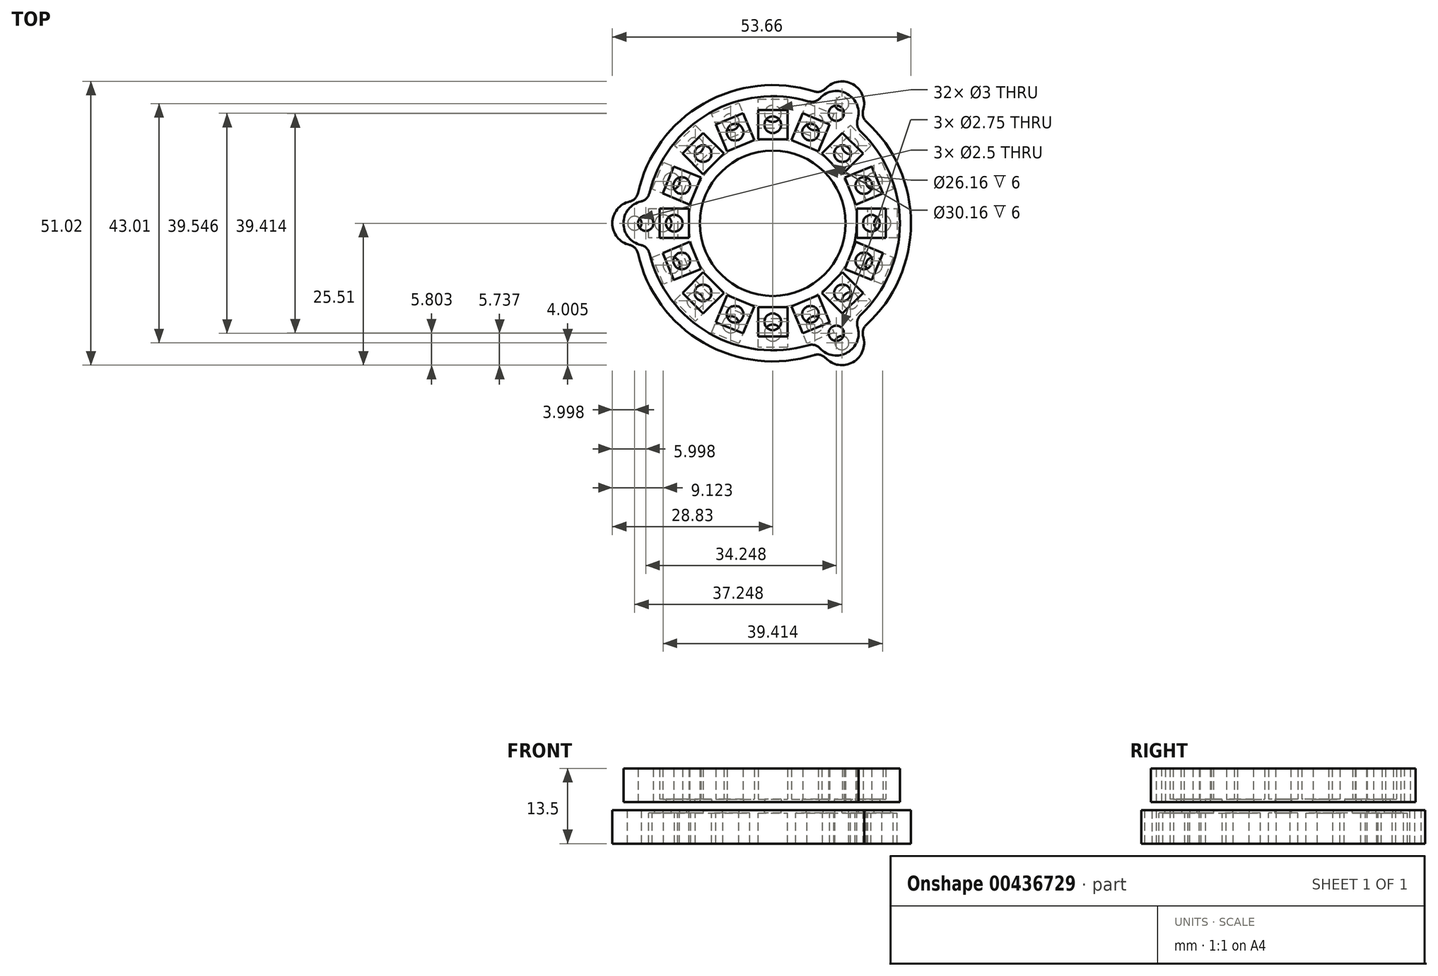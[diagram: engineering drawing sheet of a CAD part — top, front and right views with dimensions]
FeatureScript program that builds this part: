
annotation { "Feature Type Name" : "Feature", "Feature Type Description" : "" }
export const myFeature = defineFeature(function(context is Context, id is Id, definition is map)
    precondition{}
    {
        {
            var Q0;
            Q0=qCreatedBy(makeId("Top.planeOp"),FACE);
            var sketch = newSketch(context, id + "F0", { "sketchPlane" : qUnion([Q0])});
            skCircle(sketch, "E0.cCircle", {"center": v(0, 0) * mm, "radius": 15.08 * mm, "construction": true});
            skLineSegment(sketch, "E0.0", {"start": v(15.08, 3) * mm, "end": v(15.08, -3) * mm, "construction": true});
            skLineSegment(sketch, "E0.1", {"start": v(15.08, -3) * mm, "end": v(12.79, -8.54) * mm, "construction": true});
            skLineSegment(sketch, "E0.2", {"start": v(12.79, -8.54) * mm, "end": v(8.54, -12.79) * mm, "construction": true});
            skLineSegment(sketch, "E0.3", {"start": v(8.54, -12.79) * mm, "end": v(3, -15.08) * mm, "construction": true});
            skLineSegment(sketch, "E0.4", {"start": v(3, -15.08) * mm, "end": v(-3, -15.08) * mm, "construction": true});
            skLineSegment(sketch, "E0.5", {"start": v(-3, -15.08) * mm, "end": v(-8.54, -12.79) * mm, "construction": true});
            skLineSegment(sketch, "E0.6", {"start": v(-8.54, -12.79) * mm, "end": v(-12.79, -8.54) * mm, "construction": true});
            skLineSegment(sketch, "E0.7", {"start": v(-12.79, -8.54) * mm, "end": v(-15.08, -3) * mm, "construction": true});
            skLineSegment(sketch, "E0.8", {"start": v(-15.08, -3) * mm, "end": v(-15.08, 3) * mm, "construction": true});
            skLineSegment(sketch, "E0.9", {"start": v(-15.08, 3) * mm, "end": v(-12.79, 8.54) * mm, "construction": true});
            skLineSegment(sketch, "E0.10", {"start": v(-12.79, 8.54) * mm, "end": v(-8.54, 12.79) * mm, "construction": true});
            skLineSegment(sketch, "E0.11", {"start": v(-8.54, 12.79) * mm, "end": v(-3, 15.08) * mm, "construction": true});
            skLineSegment(sketch, "E0.12", {"start": v(-3, 15.08) * mm, "end": v(3, 15.08) * mm, "construction": true});
            skLineSegment(sketch, "E0.13", {"start": v(3, 15.08) * mm, "end": v(8.54, 12.79) * mm, "construction": true});
            skLineSegment(sketch, "E0.14", {"start": v(8.54, 12.79) * mm, "end": v(12.79, 8.54) * mm, "construction": true});
            skLineSegment(sketch, "E0.15", {"start": v(12.79, 8.54) * mm, "end": v(15.08, 3) * mm, "construction": true});
            skPoint(sketch, "E0.0.midPoint", {"position": v(15.08, 0) * mm});
            skLineSegment(sketch, "E1", {"start": v(13.6, 0) * mm, "end": v(23.93, 0) * mm, "construction": true});
            skLineSegment(sketch, "E2", {"start": v(15.08, 2.62) * mm, "end": v(20.33, 2.62) * mm, "construction": true});
            skLineSegment(sketch, "E3", {"start": v(20.33, 2.62) * mm, "end": v(20.33, -2.62) * mm, "construction": true});
            skLineSegment(sketch, "E4", {"start": v(20.33, -2.62) * mm, "end": v(15.08, -2.62) * mm, "construction": true});
            skLineSegment(sketch, "E5", {"start": v(17.08, 2.62) * mm, "end": v(22.33, 2.62) * mm, "construction": true});
            skLineSegment(sketch, "E6", {"start": v(22.33, 2.62) * mm, "end": v(22.33, -2.62) * mm, "construction": true});
            skLineSegment(sketch, "E7", {"start": v(22.33, -2.62) * mm, "end": v(17.08, -2.62) * mm, "construction": true});
            skLineSegment(sketch, "E8", {"start": v(17.08, -2.62) * mm, "end": v(17.08, 2.62) * mm, "construction": true});
            skSolve(sketch);
        }
        {
            var Q0;
            Q0=qCreatedBy(makeId("Top.planeOp"),FACE);
            cPlane(context, id + "F1", {"entities" : qUnion([Q0]), "cplaneType" : CPlaneType.OFFSET, "offset" : 0.5 * mm, "oppositeDirection" : true, "width" : 150 * mm, "height" : 150 * mm});
        }
        {
            var Q0;
            Q0=qCreatedBy(id+"F1.planeOp",FACE);
            var sketch = newSketch(context, id + "F2", { "sketchPlane" : qUnion([Q0])});
            skCircle(sketch, "E9", {"center": v(-22.83, 0) * mm, "radius": 1.38 * mm});
            skArc(sketch, "E10", {"start": v(-22.48, 3.98) * mm, "mid": v(-26.83, 0) * mm, "end": v(-22.48, -3.98) * mm});
            skCircle(sketch, "E11", {"center": v(17.7, 0) * mm, "radius": 1.5 * mm});
            skCircle(sketch, "E12.1.0", {"center": v(16.36, -6.78) * mm, "radius": 1.5 * mm});
            skCircle(sketch, "E12.2.0", {"center": v(12.52, -12.52) * mm, "radius": 1.5 * mm});
            skCircle(sketch, "E12.3.0", {"center": v(6.78, -16.36) * mm, "radius": 1.5 * mm});
            skCircle(sketch, "E12.4.0", {"center": v(0, -17.7) * mm, "radius": 1.5 * mm});
            skCircle(sketch, "E12.5.0", {"center": v(-6.78, -16.36) * mm, "radius": 1.5 * mm});
            skCircle(sketch, "E12.6.0", {"center": v(-12.52, -12.52) * mm, "radius": 1.5 * mm});
            skCircle(sketch, "E12.7.0", {"center": v(-16.36, -6.78) * mm, "radius": 1.5 * mm});
            skCircle(sketch, "E12.8.0", {"center": v(-17.7, 0) * mm, "radius": 1.5 * mm});
            skCircle(sketch, "E12.9.0", {"center": v(-16.36, 6.78) * mm, "radius": 1.5 * mm});
            skCircle(sketch, "E12.10.0", {"center": v(-12.52, 12.52) * mm, "radius": 1.5 * mm});
            skCircle(sketch, "E12.11.0", {"center": v(-6.78, 16.36) * mm, "radius": 1.5 * mm});
            skCircle(sketch, "E12.12.0", {"center": v(0, 17.7) * mm, "radius": 1.5 * mm});
            skCircle(sketch, "E12.13.0", {"center": v(6.78, 16.36) * mm, "radius": 1.5 * mm});
            skCircle(sketch, "E12.14.0", {"center": v(12.52, 12.52) * mm, "radius": 1.5 * mm});
            skCircle(sketch, "E12.15.0", {"center": v(16.36, 6.78) * mm, "radius": 1.5 * mm});
            skLineSegment(sketch, "E12.anchor1", {"start": v(0, 0) * mm, "end": v(17.7, 0) * mm, "construction": true});
            skLineSegment(sketch, "E12.anchor2", {"start": v(0, 0) * mm, "end": v(16.36, 6.78) * mm, "construction": true});
            skCircle(sketch, "E13.1.0", {"center": v(11.42, -19.77) * mm, "radius": 1.38 * mm});
            skArc(sketch, "E13.1.1", {"start": v(7.8, -21.46) * mm, "mid": v(13.42, -23.24) * mm, "end": v(14.7, -17.48) * mm});
            skCircle(sketch, "E13.2.0", {"center": v(11.42, 19.77) * mm, "radius": 1.38 * mm});
            skArc(sketch, "E13.2.1", {"start": v(14.7, 17.48) * mm, "mid": v(13.42, 23.24) * mm, "end": v(7.8, 21.46) * mm});
            skPoint(sketch, "E13.center", {"position": v(0, 0) * mm});
            skCircle(sketch, "E14", {"center": v(0, 0) * mm, "radius": 13.08 * mm});
            skArc(sketch, "E15.trimOffspring", {"start": v(-22.48, -3.98) * mm, "mid": v(-11.42, -19.77) * mm, "end": v(7.8, -21.46) * mm});
            skArc(sketch, "E16.trimOffspring", {"start": v(14.7, -17.48) * mm, "mid": v(22.83, 0) * mm, "end": v(14.7, 17.48) * mm});
            skArc(sketch, "E17.trimOffspring", {"start": v(7.8, 21.46) * mm, "mid": v(-11.42, 19.77) * mm, "end": v(-22.48, 3.98) * mm});
            skSolve(sketch);
        }
        {
            var Q0;
            Q0=qSketchRegion(id+"F2",true);
            extrude(context, id + "F3", {"entities" : qUnion([Q0]), "depth" : 6 * mm, "offsetDistance" : 25 * mm});
        }
        {
            var Q0;
            Q0=qCreatedBy(makeId("Top.planeOp"),FACE);
            var sketch = newSketch(context, id + "F4", { "sketchPlane" : qUnion([Q0])});
            skLineSegment(sketch, "E18.0", {"start": v(15.08, 2.62) * mm, "end": v(20.33, 2.62) * mm});
            skLineSegment(sketch, "E19.0", {"start": v(20.33, 2.62) * mm, "end": v(20.33, -2.62) * mm});
            skLineSegment(sketch, "E20.0", {"start": v(20.33, -2.62) * mm, "end": v(15.08, -2.62) * mm});
            skLineSegment(sketch, "E21", {"start": v(15.08, 2.62) * mm, "end": v(15.08, -2.62) * mm});
            skLineSegment(sketch, "E22.1.0", {"start": v(12.93, 8.2) * mm, "end": v(17.78, 10.2) * mm});
            skLineSegment(sketch, "E22.1.1", {"start": v(12.93, 8.2) * mm, "end": v(14.94, 3.35) * mm});
            skLineSegment(sketch, "E22.1.2", {"start": v(19.79, 5.36) * mm, "end": v(14.94, 3.35) * mm});
            skLineSegment(sketch, "E22.1.3", {"start": v(17.78, 10.2) * mm, "end": v(19.79, 5.36) * mm});
            skLineSegment(sketch, "E22.2.0", {"start": v(8.8, 12.52) * mm, "end": v(12.52, 16.23) * mm});
            skLineSegment(sketch, "E22.2.1", {"start": v(8.8, 12.52) * mm, "end": v(12.52, 8.8) * mm});
            skLineSegment(sketch, "E22.2.2", {"start": v(16.23, 12.52) * mm, "end": v(12.52, 8.8) * mm});
            skLineSegment(sketch, "E22.2.3", {"start": v(12.52, 16.23) * mm, "end": v(16.23, 12.52) * mm});
            skLineSegment(sketch, "E22.3.0", {"start": v(3.35, 14.94) * mm, "end": v(5.36, 19.79) * mm});
            skLineSegment(sketch, "E22.3.1", {"start": v(3.35, 14.94) * mm, "end": v(8.2, 12.93) * mm});
            skLineSegment(sketch, "E22.3.2", {"start": v(10.2, 17.78) * mm, "end": v(8.2, 12.93) * mm});
            skLineSegment(sketch, "E22.3.3", {"start": v(5.36, 19.79) * mm, "end": v(10.2, 17.78) * mm});
            skLineSegment(sketch, "E22.4.0", {"start": v(-2.62, 15.08) * mm, "end": v(-2.62, 20.33) * mm});
            skLineSegment(sketch, "E22.4.1", {"start": v(-2.62, 15.08) * mm, "end": v(2.63, 15.08) * mm});
            skLineSegment(sketch, "E22.4.2", {"start": v(2.62, 20.33) * mm, "end": v(2.63, 15.08) * mm});
            skLineSegment(sketch, "E22.4.3", {"start": v(-2.62, 20.33) * mm, "end": v(2.63, 20.33) * mm});
            skLineSegment(sketch, "E22.5.0", {"start": v(-8.2, 12.93) * mm, "end": v(-10.2, 17.78) * mm});
            skLineSegment(sketch, "E22.5.1", {"start": v(-8.2, 12.93) * mm, "end": v(-3.35, 14.94) * mm});
            skLineSegment(sketch, "E22.5.2", {"start": v(-5.36, 19.79) * mm, "end": v(-3.35, 14.94) * mm});
            skLineSegment(sketch, "E22.5.3", {"start": v(-10.2, 17.78) * mm, "end": v(-5.36, 19.79) * mm});
            skLineSegment(sketch, "E22.6.0", {"start": v(-12.52, 8.8) * mm, "end": v(-16.23, 12.52) * mm});
            skLineSegment(sketch, "E22.6.1", {"start": v(-12.52, 8.8) * mm, "end": v(-8.8, 12.52) * mm});
            skLineSegment(sketch, "E22.6.2", {"start": v(-12.52, 16.23) * mm, "end": v(-8.8, 12.52) * mm});
            skLineSegment(sketch, "E22.6.3", {"start": v(-16.23, 12.52) * mm, "end": v(-12.52, 16.23) * mm});
            skLineSegment(sketch, "E22.7.0", {"start": v(-14.94, 3.35) * mm, "end": v(-19.79, 5.36) * mm});
            skLineSegment(sketch, "E22.7.1", {"start": v(-14.94, 3.35) * mm, "end": v(-12.93, 8.2) * mm});
            skLineSegment(sketch, "E22.7.2", {"start": v(-17.78, 10.2) * mm, "end": v(-12.93, 8.2) * mm});
            skLineSegment(sketch, "E22.7.3", {"start": v(-19.79, 5.36) * mm, "end": v(-17.78, 10.2) * mm});
            skLineSegment(sketch, "E22.8.0", {"start": v(-15.08, -2.62) * mm, "end": v(-20.33, -2.62) * mm});
            skLineSegment(sketch, "E22.8.1", {"start": v(-15.08, -2.62) * mm, "end": v(-15.08, 2.63) * mm});
            skLineSegment(sketch, "E22.8.2", {"start": v(-20.33, 2.63) * mm, "end": v(-15.08, 2.63) * mm});
            skLineSegment(sketch, "E22.8.3", {"start": v(-20.33, -2.62) * mm, "end": v(-20.33, 2.63) * mm});
            skLineSegment(sketch, "E22.9.0", {"start": v(-12.93, -8.2) * mm, "end": v(-17.78, -10.2) * mm});
            skLineSegment(sketch, "E22.9.1", {"start": v(-12.93, -8.2) * mm, "end": v(-14.94, -3.35) * mm});
            skLineSegment(sketch, "E22.9.2", {"start": v(-19.79, -5.36) * mm, "end": v(-14.94, -3.35) * mm});
            skLineSegment(sketch, "E22.9.3", {"start": v(-17.78, -10.2) * mm, "end": v(-19.79, -5.36) * mm});
            skLineSegment(sketch, "E22.10.0", {"start": v(-8.8, -12.52) * mm, "end": v(-12.52, -16.23) * mm});
            skLineSegment(sketch, "E22.10.1", {"start": v(-8.8, -12.52) * mm, "end": v(-12.52, -8.8) * mm});
            skLineSegment(sketch, "E22.10.2", {"start": v(-16.23, -12.52) * mm, "end": v(-12.52, -8.8) * mm});
            skLineSegment(sketch, "E22.10.3", {"start": v(-12.52, -16.23) * mm, "end": v(-16.23, -12.52) * mm});
            skLineSegment(sketch, "E22.11.0", {"start": v(-3.35, -14.94) * mm, "end": v(-5.36, -19.79) * mm});
            skLineSegment(sketch, "E22.11.1", {"start": v(-3.35, -14.94) * mm, "end": v(-8.2, -12.93) * mm});
            skLineSegment(sketch, "E22.11.2", {"start": v(-10.2, -17.78) * mm, "end": v(-8.2, -12.93) * mm});
            skLineSegment(sketch, "E22.11.3", {"start": v(-5.36, -19.79) * mm, "end": v(-10.2, -17.78) * mm});
            skLineSegment(sketch, "E22.12.0", {"start": v(2.62, -15.08) * mm, "end": v(2.62, -20.33) * mm});
            skLineSegment(sketch, "E22.12.1", {"start": v(2.62, -15.08) * mm, "end": v(-2.63, -15.08) * mm});
            skLineSegment(sketch, "E22.12.2", {"start": v(-2.63, -20.33) * mm, "end": v(-2.63, -15.08) * mm});
            skLineSegment(sketch, "E22.12.3", {"start": v(2.62, -20.33) * mm, "end": v(-2.63, -20.33) * mm});
            skLineSegment(sketch, "E22.13.0", {"start": v(8.2, -12.93) * mm, "end": v(10.2, -17.78) * mm});
            skLineSegment(sketch, "E22.13.1", {"start": v(8.2, -12.93) * mm, "end": v(3.35, -14.94) * mm});
            skLineSegment(sketch, "E22.13.2", {"start": v(5.36, -19.79) * mm, "end": v(3.35, -14.94) * mm});
            skLineSegment(sketch, "E22.13.3", {"start": v(10.2, -17.78) * mm, "end": v(5.36, -19.79) * mm});
            skLineSegment(sketch, "E22.14.0", {"start": v(12.52, -8.8) * mm, "end": v(16.23, -12.52) * mm});
            skLineSegment(sketch, "E22.14.1", {"start": v(12.52, -8.8) * mm, "end": v(8.8, -12.52) * mm});
            skLineSegment(sketch, "E22.14.2", {"start": v(12.52, -16.23) * mm, "end": v(8.8, -12.52) * mm});
            skLineSegment(sketch, "E22.14.3", {"start": v(16.23, -12.52) * mm, "end": v(12.52, -16.23) * mm});
            skLineSegment(sketch, "E22.15.0", {"start": v(14.94, -3.35) * mm, "end": v(19.79, -5.36) * mm});
            skLineSegment(sketch, "E22.15.1", {"start": v(14.94, -3.35) * mm, "end": v(12.93, -8.2) * mm});
            skLineSegment(sketch, "E22.15.2", {"start": v(17.78, -10.2) * mm, "end": v(12.93, -8.2) * mm});
            skLineSegment(sketch, "E22.15.3", {"start": v(19.79, -5.36) * mm, "end": v(17.78, -10.2) * mm});
            skPoint(sketch, "E22.center", {"position": v(0, 0) * mm});
            skSolve(sketch);
        }
        {
            var Q0;
            Q0=qSketchRegion(id+"F4",true);
            extrude(context, id + "F5", {"entities" : qUnion([Q0]), "operationType" : NewBodyOperationType.REMOVE, "depth" : 6 * mm, "offsetDistance" : 25 * mm});
        }
        {
            var Q0;
            Q0=qCreatedBy(makeId("Top.planeOp"),FACE);
            cPlane(context, id + "F6", {"entities" : qUnion([Q0]), "cplaneType" : CPlaneType.OFFSET, "offset" : 2 * mm, "oppositeDirection" : true, "width" : 150 * mm, "height" : 150 * mm});
        }
        {
            var Q0;
            Q0=qCreatedBy(id+"F6.planeOp",FACE);
            var sketch = newSketch(context, id + "F7", { "sketchPlane" : qUnion([Q0])});
            skCircle(sketch, "E23", {"center": v(0, 0) * mm, "radius": 15.08 * mm});
            skArc(sketch, "E24", {"start": v(-24.5, -3.99) * mm, "mid": v(-12.42, -21.5) * mm, "end": v(8.8, -23.22) * mm});
            skArc(sketch, "E25", {"start": v(-24.5, 3.99) * mm, "mid": v(-28.83, 0) * mm, "end": v(-24.5, -3.99) * mm});
            skCircle(sketch, "E26", {"center": v(-24.83, 0) * mm, "radius": 1.25 * mm});
            skArc(sketch, "E27.1.0", {"start": v(8.8, -23.22) * mm, "mid": v(14.42, -24.97) * mm, "end": v(15.7, -19.23) * mm});
            skCircle(sketch, "E27.1.1", {"center": v(12.42, -21.5) * mm, "radius": 1.25 * mm});
            skArc(sketch, "E27.2.0", {"start": v(15.7, 19.23) * mm, "mid": v(14.42, 24.97) * mm, "end": v(8.8, 23.22) * mm});
            skCircle(sketch, "E27.2.1", {"center": v(12.42, 21.5) * mm, "radius": 1.25 * mm});
            skCircle(sketch, "E28", {"center": v(19.7, 0) * mm, "radius": 1.5 * mm});
            skCircle(sketch, "E29.1.0", {"center": v(18.2, 7.54) * mm, "radius": 1.5 * mm});
            skCircle(sketch, "E29.2.0", {"center": v(13.93, 13.93) * mm, "radius": 1.5 * mm});
            skCircle(sketch, "E29.3.0", {"center": v(7.54, 18.2) * mm, "radius": 1.5 * mm});
            skCircle(sketch, "E29.4.0", {"center": v(0, 19.7) * mm, "radius": 1.5 * mm});
            skCircle(sketch, "E29.5.0", {"center": v(-7.54, 18.2) * mm, "radius": 1.5 * mm});
            skCircle(sketch, "E29.6.0", {"center": v(-13.93, 13.93) * mm, "radius": 1.5 * mm});
            skCircle(sketch, "E29.7.0", {"center": v(-18.2, 7.54) * mm, "radius": 1.5 * mm});
            skCircle(sketch, "E29.8.0", {"center": v(-19.7, 0) * mm, "radius": 1.5 * mm});
            skCircle(sketch, "E29.9.0", {"center": v(-18.2, -7.54) * mm, "radius": 1.5 * mm});
            skCircle(sketch, "E29.10.0", {"center": v(-13.93, -13.93) * mm, "radius": 1.5 * mm});
            skCircle(sketch, "E29.11.0", {"center": v(-7.54, -18.2) * mm, "radius": 1.5 * mm});
            skCircle(sketch, "E29.12.0", {"center": v(0, -19.7) * mm, "radius": 1.5 * mm});
            skCircle(sketch, "E29.13.0", {"center": v(7.54, -18.2) * mm, "radius": 1.5 * mm});
            skCircle(sketch, "E29.14.0", {"center": v(13.93, -13.93) * mm, "radius": 1.5 * mm});
            skCircle(sketch, "E29.15.0", {"center": v(18.2, -7.54) * mm, "radius": 1.5 * mm});
            skArc(sketch, "E30.trimOffspring", {"start": v(8.8, 23.22) * mm, "mid": v(-12.42, 21.5) * mm, "end": v(-24.5, 3.99) * mm});
            skArc(sketch, "E31.trimOffspring", {"start": v(15.7, -19.23) * mm, "mid": v(24.83, 0) * mm, "end": v(15.7, 19.23) * mm});
            skSolve(sketch);
        }
        {
            var Q0;
            Q0 = qSketchRegion(id + "F7", true);
            extrude(context, id + "F8", {"entities" : qUnion([Q0]), "oppositeDirection" : true, "depth" : 6 * mm, "offsetDistance" : 25 * mm});
        }
        {
            var Q0;
            Q0=makeQuery(id+"F8.opExtrude","CAP_FACE",FACE,{"disambiguationData":[OSD([sQuery(id+"F7.wireOp",EDGE,"E23"),sQuery(id+"F7.wireOp",EDGE,"E24"),sQuery(id+"F7.wireOp",EDGE,"E25"),sQuery(id+"F7.wireOp",EDGE,"E26"),sQuery(id+"F7.wireOp",EDGE,"E27.1.0"),sQuery(id+"F7.wireOp",EDGE,"E27.1.1"),sQuery(id+"F7.wireOp",EDGE,"E27.2.0"),sQuery(id+"F7.wireOp",EDGE,"E27.2.1")])],"isStart":true});
            cPlane(context, id + "F9", {"entities" : qUnion([Q0]), "cplaneType" : CPlaneType.OFFSET, "offset" : 0.5 * mm, "oppositeDirection" : true, "width" : 150 * mm, "height" : 150 * mm});
        }
        {
            var Q0;
            Q0=qCreatedBy(id+"F9.planeOp",FACE);
            var sketch = newSketch(context, id + "F10", { "sketchPlane" : qUnion([Q0])});
            skLineSegment(sketch, "E32.0", {"start": v(17.08, 2.62) * mm, "end": v(22.33, 2.62) * mm});
            skLineSegment(sketch, "E33.0", {"start": v(22.33, 2.62) * mm, "end": v(22.33, -2.62) * mm});
            skLineSegment(sketch, "E34.0", {"start": v(22.33, -2.62) * mm, "end": v(17.08, -2.62) * mm});
            skLineSegment(sketch, "E35.0", {"start": v(17.08, -2.62) * mm, "end": v(17.08, 2.62) * mm});
            skLineSegment(sketch, "E36.1.0", {"start": v(14.78, 8.96) * mm, "end": v(19.63, 10.97) * mm});
            skLineSegment(sketch, "E36.1.1", {"start": v(16.79, 4.11) * mm, "end": v(14.78, 8.96) * mm});
            skLineSegment(sketch, "E36.1.2", {"start": v(21.64, 6.12) * mm, "end": v(16.79, 4.11) * mm});
            skLineSegment(sketch, "E36.1.3", {"start": v(19.63, 10.97) * mm, "end": v(21.64, 6.12) * mm});
            skLineSegment(sketch, "E36.2.0", {"start": v(10.22, 13.93) * mm, "end": v(13.93, 17.65) * mm});
            skLineSegment(sketch, "E36.2.1", {"start": v(13.93, 10.22) * mm, "end": v(10.22, 13.93) * mm});
            skLineSegment(sketch, "E36.2.2", {"start": v(17.65, 13.93) * mm, "end": v(13.93, 10.22) * mm});
            skLineSegment(sketch, "E36.2.3", {"start": v(13.93, 17.65) * mm, "end": v(17.65, 13.93) * mm});
            skLineSegment(sketch, "E36.3.0", {"start": v(4.11, 16.79) * mm, "end": v(6.12, 21.64) * mm});
            skLineSegment(sketch, "E36.3.1", {"start": v(8.96, 14.78) * mm, "end": v(4.11, 16.79) * mm});
            skLineSegment(sketch, "E36.3.2", {"start": v(10.97, 19.63) * mm, "end": v(8.96, 14.78) * mm});
            skLineSegment(sketch, "E36.3.3", {"start": v(6.12, 21.64) * mm, "end": v(10.97, 19.63) * mm});
            skLineSegment(sketch, "E36.4.0", {"start": v(-2.62, 17.08) * mm, "end": v(-2.62, 22.33) * mm});
            skLineSegment(sketch, "E36.4.1", {"start": v(2.63, 17.08) * mm, "end": v(-2.62, 17.08) * mm});
            skLineSegment(sketch, "E36.4.2", {"start": v(2.63, 22.33) * mm, "end": v(2.63, 17.08) * mm});
            skLineSegment(sketch, "E36.4.3", {"start": v(-2.62, 22.33) * mm, "end": v(2.63, 22.33) * mm});
            skLineSegment(sketch, "E36.5.0", {"start": v(-8.96, 14.78) * mm, "end": v(-10.97, 19.63) * mm});
            skLineSegment(sketch, "E36.5.1", {"start": v(-4.11, 16.79) * mm, "end": v(-8.96, 14.78) * mm});
            skLineSegment(sketch, "E36.5.2", {"start": v(-6.12, 21.64) * mm, "end": v(-4.11, 16.79) * mm});
            skLineSegment(sketch, "E36.5.3", {"start": v(-10.97, 19.63) * mm, "end": v(-6.12, 21.64) * mm});
            skLineSegment(sketch, "E36.6.0", {"start": v(-13.93, 10.22) * mm, "end": v(-17.65, 13.93) * mm});
            skLineSegment(sketch, "E36.6.1", {"start": v(-10.22, 13.93) * mm, "end": v(-13.93, 10.22) * mm});
            skLineSegment(sketch, "E36.6.2", {"start": v(-13.93, 17.65) * mm, "end": v(-10.22, 13.93) * mm});
            skLineSegment(sketch, "E36.6.3", {"start": v(-17.65, 13.93) * mm, "end": v(-13.93, 17.65) * mm});
            skLineSegment(sketch, "E36.7.0", {"start": v(-16.79, 4.11) * mm, "end": v(-21.64, 6.12) * mm});
            skLineSegment(sketch, "E36.7.1", {"start": v(-14.78, 8.96) * mm, "end": v(-16.79, 4.11) * mm});
            skLineSegment(sketch, "E36.7.2", {"start": v(-19.63, 10.97) * mm, "end": v(-14.78, 8.96) * mm});
            skLineSegment(sketch, "E36.7.3", {"start": v(-21.64, 6.12) * mm, "end": v(-19.63, 10.97) * mm});
            skLineSegment(sketch, "E36.8.0", {"start": v(-17.08, -2.62) * mm, "end": v(-22.33, -2.62) * mm});
            skLineSegment(sketch, "E36.8.1", {"start": v(-17.08, 2.63) * mm, "end": v(-17.08, -2.62) * mm});
            skLineSegment(sketch, "E36.8.2", {"start": v(-22.33, 2.63) * mm, "end": v(-17.08, 2.63) * mm});
            skLineSegment(sketch, "E36.8.3", {"start": v(-22.33, -2.62) * mm, "end": v(-22.33, 2.63) * mm});
            skLineSegment(sketch, "E36.9.0", {"start": v(-14.78, -8.96) * mm, "end": v(-19.63, -10.97) * mm});
            skLineSegment(sketch, "E36.9.1", {"start": v(-16.79, -4.11) * mm, "end": v(-14.78, -8.96) * mm});
            skLineSegment(sketch, "E36.9.2", {"start": v(-21.64, -6.12) * mm, "end": v(-16.79, -4.11) * mm});
            skLineSegment(sketch, "E36.9.3", {"start": v(-19.63, -10.97) * mm, "end": v(-21.64, -6.12) * mm});
            skLineSegment(sketch, "E36.10.0", {"start": v(-10.22, -13.93) * mm, "end": v(-13.93, -17.65) * mm});
            skLineSegment(sketch, "E36.10.1", {"start": v(-13.93, -10.22) * mm, "end": v(-10.22, -13.93) * mm});
            skLineSegment(sketch, "E36.10.2", {"start": v(-17.65, -13.93) * mm, "end": v(-13.93, -10.22) * mm});
            skLineSegment(sketch, "E36.10.3", {"start": v(-13.93, -17.65) * mm, "end": v(-17.65, -13.93) * mm});
            skLineSegment(sketch, "E36.11.0", {"start": v(-4.11, -16.79) * mm, "end": v(-6.12, -21.64) * mm});
            skLineSegment(sketch, "E36.11.1", {"start": v(-8.96, -14.78) * mm, "end": v(-4.11, -16.79) * mm});
            skLineSegment(sketch, "E36.11.2", {"start": v(-10.97, -19.63) * mm, "end": v(-8.96, -14.78) * mm});
            skLineSegment(sketch, "E36.11.3", {"start": v(-6.12, -21.64) * mm, "end": v(-10.97, -19.63) * mm});
            skLineSegment(sketch, "E36.12.0", {"start": v(2.62, -17.08) * mm, "end": v(2.62, -22.33) * mm});
            skLineSegment(sketch, "E36.12.1", {"start": v(-2.63, -17.08) * mm, "end": v(2.62, -17.08) * mm});
            skLineSegment(sketch, "E36.12.2", {"start": v(-2.63, -22.33) * mm, "end": v(-2.63, -17.08) * mm});
            skLineSegment(sketch, "E36.12.3", {"start": v(2.62, -22.33) * mm, "end": v(-2.63, -22.33) * mm});
            skLineSegment(sketch, "E36.13.0", {"start": v(8.96, -14.78) * mm, "end": v(10.97, -19.63) * mm});
            skLineSegment(sketch, "E36.13.1", {"start": v(4.11, -16.79) * mm, "end": v(8.96, -14.78) * mm});
            skLineSegment(sketch, "E36.13.2", {"start": v(6.12, -21.64) * mm, "end": v(4.11, -16.79) * mm});
            skLineSegment(sketch, "E36.13.3", {"start": v(10.97, -19.63) * mm, "end": v(6.12, -21.64) * mm});
            skLineSegment(sketch, "E36.14.0", {"start": v(13.93, -10.22) * mm, "end": v(17.65, -13.93) * mm});
            skLineSegment(sketch, "E36.14.1", {"start": v(10.22, -13.93) * mm, "end": v(13.93, -10.22) * mm});
            skLineSegment(sketch, "E36.14.2", {"start": v(13.93, -17.65) * mm, "end": v(10.22, -13.93) * mm});
            skLineSegment(sketch, "E36.14.3", {"start": v(17.65, -13.93) * mm, "end": v(13.93, -17.65) * mm});
            skLineSegment(sketch, "E36.15.0", {"start": v(16.79, -4.11) * mm, "end": v(21.64, -6.12) * mm});
            skLineSegment(sketch, "E36.15.1", {"start": v(14.78, -8.96) * mm, "end": v(16.79, -4.11) * mm});
            skLineSegment(sketch, "E36.15.2", {"start": v(19.63, -10.97) * mm, "end": v(14.78, -8.96) * mm});
            skLineSegment(sketch, "E36.15.3", {"start": v(21.64, -6.12) * mm, "end": v(19.63, -10.97) * mm});
            skPoint(sketch, "E36.center", {"position": v(0, 0) * mm});
            skSolve(sketch);
        }
        {
            var Q0;
            Q0 = qSketchRegion(id + "F10", true);
            extrude(context, id + "F11", {"entities" : qUnion([Q0]), "operationType" : NewBodyOperationType.REMOVE, "oppositeDirection" : true, "depth" : 6 * mm, "offsetDistance" : 25 * mm});
        }
        {
            var Q0;
            Q0=makeQuery(id+"F8.opExtrude","SWEPT_EDGE",EDGE,{"disambiguationData":[OSD([sQuery(id+"F7.wireOp",EDGE,"E27.2.0"),sQuery(id+"F7.wireOp",EDGE,"E30.trimOffspring")])]});
            var Q1;
            Q1=makeQuery(id+"F8.opExtrude","SWEPT_EDGE",EDGE,{"disambiguationData":[OSD([sQuery(id+"F7.wireOp",EDGE,"E27.2.0"),sQuery(id+"F7.wireOp",EDGE,"E31.trimOffspring")])]});
            var Q2;
            Q2=makeQuery(id+"F8.opExtrude","SWEPT_EDGE",EDGE,{"disambiguationData":[OSD([sQuery(id+"F7.wireOp",EDGE,"E27.1.0"),sQuery(id+"F7.wireOp",EDGE,"E31.trimOffspring")])]});
            var Q3;
            Q3=makeQuery(id+"F8.opExtrude","SWEPT_EDGE",EDGE,{"disambiguationData":[OSD([sQuery(id+"F7.wireOp",EDGE,"E24"),sQuery(id+"F7.wireOp",EDGE,"E27.1.0")])]});
            var Q4;
            Q4=makeQuery(id+"F8.opExtrude","SWEPT_EDGE",EDGE,{"disambiguationData":[OSD([sQuery(id+"F7.wireOp",EDGE,"E24"),sQuery(id+"F7.wireOp",EDGE,"E25")])]});
            var Q5;
            Q5=makeQuery(id+"F8.opExtrude","SWEPT_EDGE",EDGE,{"disambiguationData":[OSD([sQuery(id+"F7.wireOp",EDGE,"E25"),sQuery(id+"F7.wireOp",EDGE,"E30.trimOffspring")])]});
            var Q6;
            Q6=makeQuery(id+"F3.opExtrude","SWEPT_EDGE",EDGE,{"disambiguationData":[OSD([sQuery(id+"F2.wireOp",EDGE,"E10"),sQuery(id+"F2.wireOp",EDGE,"E17.trimOffspring")])]});
            var Q7;
            Q7=makeQuery(id+"F3.opExtrude","SWEPT_EDGE",EDGE,{"disambiguationData":[OSD([sQuery(id+"F2.wireOp",EDGE,"E10"),sQuery(id+"F2.wireOp",EDGE,"E15.trimOffspring")])]});
            var Q8;
            Q8=makeQuery(id+"F3.opExtrude","SWEPT_EDGE",EDGE,{"disambiguationData":[OSD([sQuery(id+"F2.wireOp",EDGE,"E13.1.1"),sQuery(id+"F2.wireOp",EDGE,"E15.trimOffspring")])]});
            var Q9;
            Q9=makeQuery(id+"F3.opExtrude","SWEPT_EDGE",EDGE,{"disambiguationData":[OSD([sQuery(id+"F2.wireOp",EDGE,"E13.1.1"),sQuery(id+"F2.wireOp",EDGE,"E16.trimOffspring")])]});
            var Q10;
            Q10=makeQuery(id+"F3.opExtrude","SWEPT_EDGE",EDGE,{"disambiguationData":[OSD([sQuery(id+"F2.wireOp",EDGE,"E13.2.1"),sQuery(id+"F2.wireOp",EDGE,"E16.trimOffspring")])]});
            var Q11;
            Q11=makeQuery(id+"F3.opExtrude","SWEPT_EDGE",EDGE,{"disambiguationData":[OSD([sQuery(id+"F2.wireOp",EDGE,"E13.2.1"),sQuery(id+"F2.wireOp",EDGE,"E17.trimOffspring")])]});
            fillet(context, id + "F12", {"entities" : qUnion([Q0, Q1, Q2, Q3, Q4, Q5, Q6, Q7, Q8, Q9, Q10, Q11]), "radius" : 2 * mm, "tangentPropagation" : true, "allowEdgeOverflow" : false});
        }
    });
